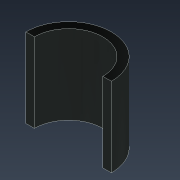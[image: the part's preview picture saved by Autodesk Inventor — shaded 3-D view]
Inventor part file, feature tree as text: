
AUTODESK INVENTOR PART (.ipt)
format: ipt  version: 2022 (Build 260153000, 153)  size: 87,552 bytes
history: native  units: mm
features: extrude x1, sketch x1
ambient origin geometry x8: Origin, YZ Plane, XZ Plane, XY Plane, X Axis, Y Axis, Z Axis, Center Point
bodies: Solid1 (feature_tree)
feature tree (2):
  extrude  "Extrusion1"  Depth=23.172mm
  sketch  "Sketch1"  dims[d0=20.0mm d1=25.0mm d2=23.172mm d3=0.0mm]
